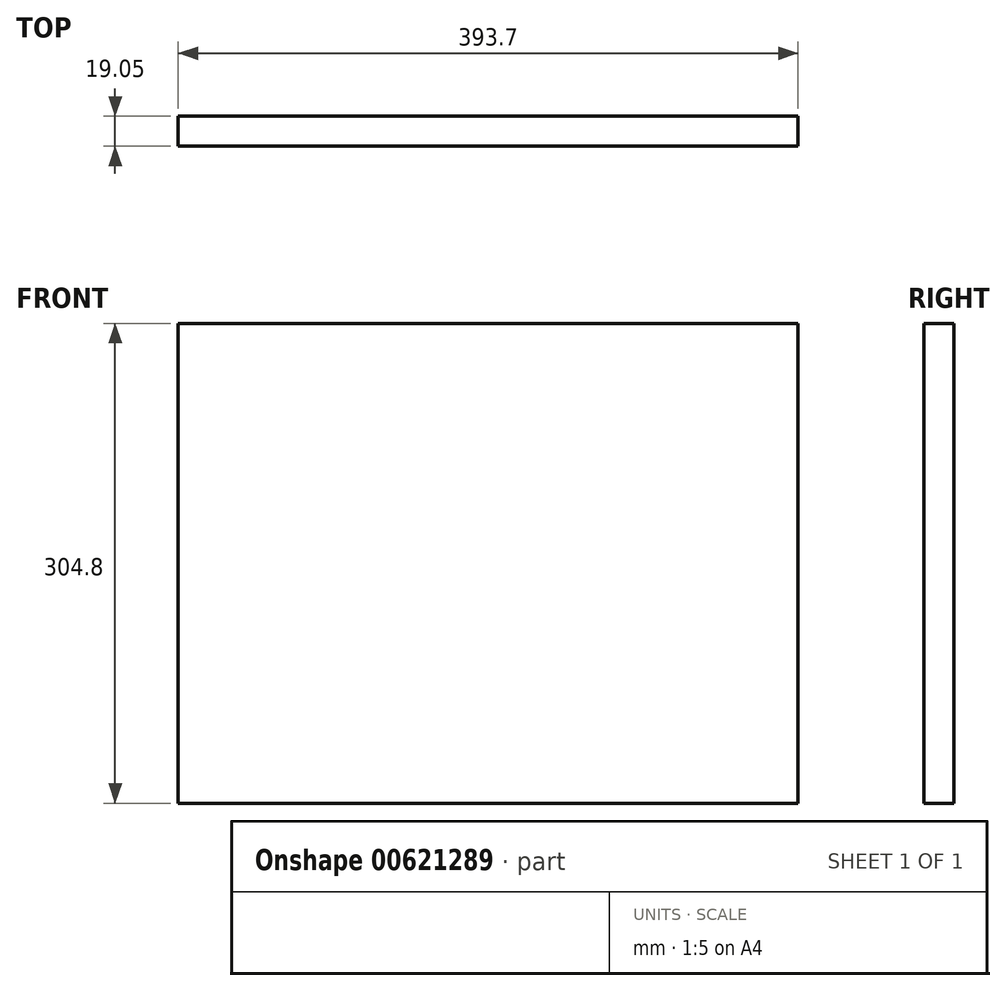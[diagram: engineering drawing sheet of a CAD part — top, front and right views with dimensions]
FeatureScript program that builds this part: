
annotation { "Feature Type Name" : "Feature", "Feature Type Description" : "" }
export const myFeature = defineFeature(function(context is Context, id is Id, definition is map)
    precondition{}
    {
        {
            var Q0;
            Q0=qCreatedBy(makeId("Front.planeOp"),FACE);
            var sketch = newSketch(context, id + "F0", { "sketchPlane" : qUnion([Q0])});
            skLineSegment(sketch, "E0.bottom", {"start": v(196.85, 152.4) * mm, "end": v(-196.85, 152.4) * mm});
            skLineSegment(sketch, "E0.top", {"start": v(196.85, -152.4) * mm, "end": v(-196.85, -152.4) * mm});
            skLineSegment(sketch, "E0.left", {"start": v(196.85, 152.4) * mm, "end": v(196.85, -152.4) * mm});
            skLineSegment(sketch, "E0.right", {"start": v(-196.85, 152.4) * mm, "end": v(-196.85, -152.4) * mm});
            skPoint(sketch, "E0.middle", {"position": v(0, 0) * mm});
            skSolve(sketch);
        }
        {
            var Q0;
            Q0=makeQuery(id+"F0.imprint","IMPRINT",FACE,{"disambiguationData":[TD([[makeQuery(id+"F0.imprint","IMPRINT",EDGE,{"derivedFrom":sQuery(id+"F0.wireOp",EDGE,"E0.bottom")}),1.0]])]});
            extrude(context, id + "F1", {"entities" : qUnion([Q0]), "depth" : 19.05 * mm, "offsetDistance" : 25.4 * mm});
        }
    });
